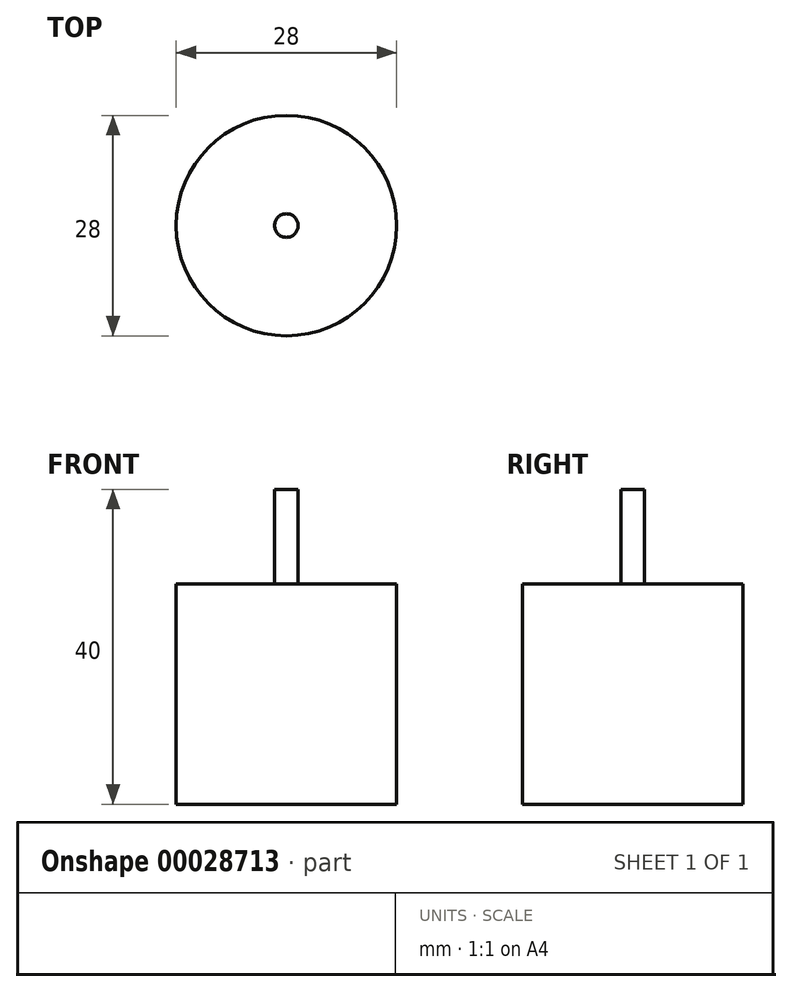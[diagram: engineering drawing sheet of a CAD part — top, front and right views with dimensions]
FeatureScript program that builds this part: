
annotation { "Feature Type Name" : "Feature", "Feature Type Description" : "" }
export const myFeature = defineFeature(function(context is Context, id is Id, definition is map)
    precondition{}
    {
        {
            var Q0;
            Q0=qCreatedBy(makeId("Front.planeOp"),FACE);
            var sketch = newSketch(context, id + "F0", { "sketchPlane" : qUnion([Q0])});
            skLineSegment(sketch, "E0", {"start": v(0, 0) * mm, "end": v(0, 44.29) * mm, "construction": true});
            skLineSegment(sketch, "E1", {"start": v(0, 40) * mm, "end": v(1.5, 40) * mm});
            skLineSegment(sketch, "E2", {"start": v(1.5, 40) * mm, "end": v(1.5, 28) * mm});
            skLineSegment(sketch, "E3", {"start": v(1.5, 28) * mm, "end": v(14, 28) * mm});
            skLineSegment(sketch, "E4", {"start": v(14, 28) * mm, "end": v(14, 0) * mm});
            skLineSegment(sketch, "E5", {"start": v(14, 0) * mm, "end": v(0, 0) * mm});
            skLineSegment(sketch, "E6", {"start": v(0, 40) * mm, "end": v(0, 0) * mm});
            skSolve(sketch);
        }
        {
            var Q0;
            Q0 = qSketchRegion(id + "F0", true);
            var Q1;
            Q1=sQuery(id+"F0.wireOp",EDGE,"E0");
            revolve(context, id + "F1", {"surfaceOperationType" : NewSurfaceOperationType.NEW, "entities" : qUnion([Q0]), "axis" : qUnion([Q1]), "revolveType" : RevolveType.FULL});
        }
    });
